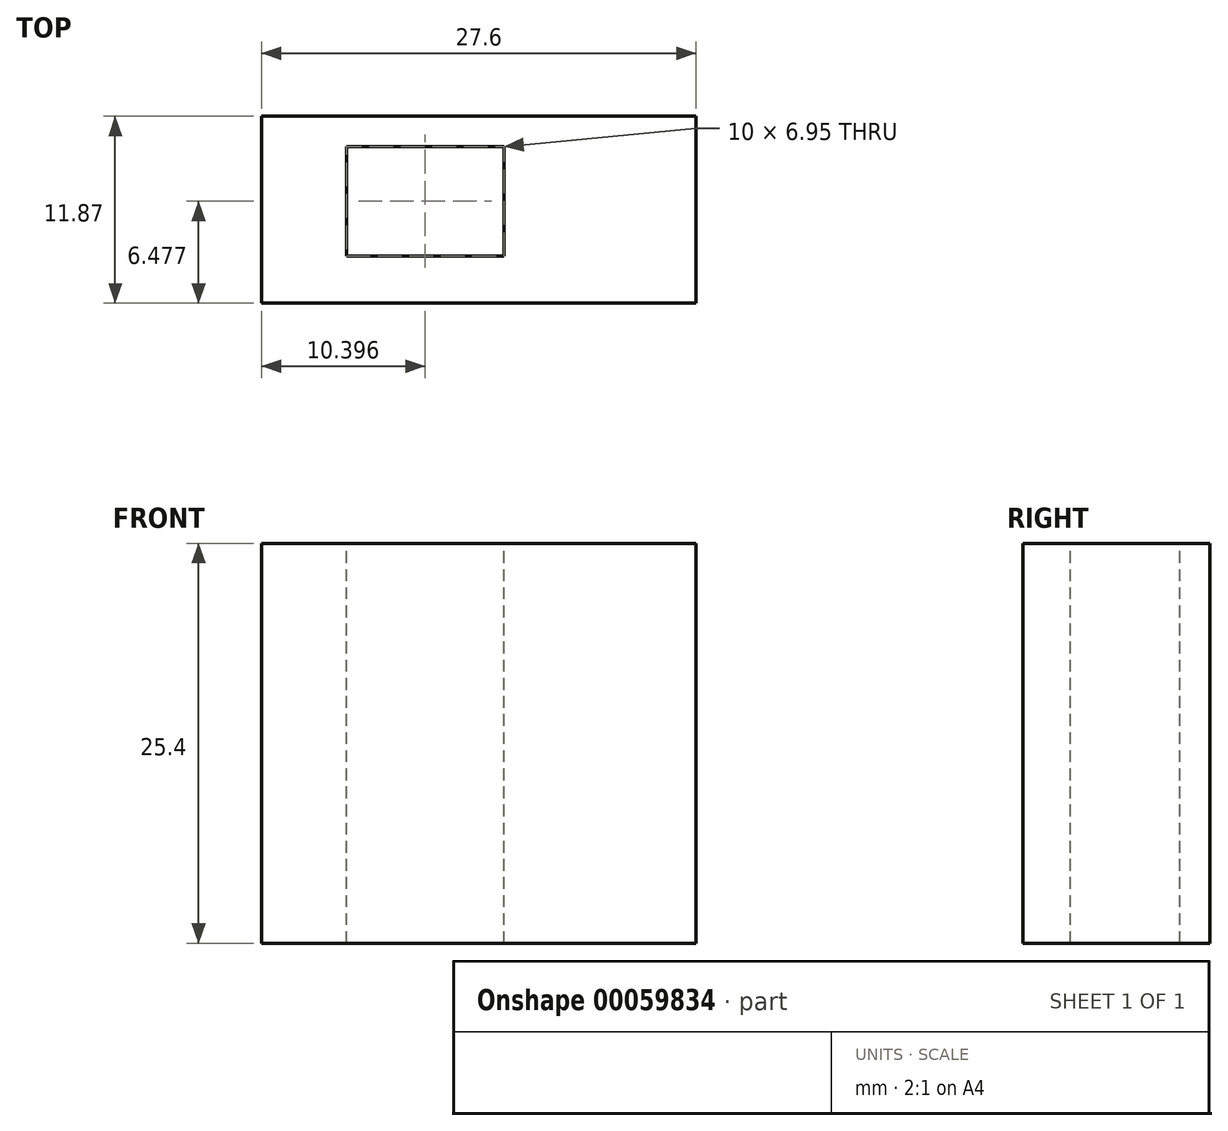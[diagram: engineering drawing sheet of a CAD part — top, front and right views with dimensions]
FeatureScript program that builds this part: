
annotation { "Feature Type Name" : "Feature", "Feature Type Description" : "" }
export const myFeature = defineFeature(function(context is Context, id is Id, definition is map)
    precondition{}
    {
        {
            var Q0;
            Q0=qCreatedBy(makeId("Top.planeOp"),FACE);
            var sketch = newSketch(context, id + "F0", { "sketchPlane" : qUnion([Q0])});
            skLineSegment(sketch, "E0.bottom", {"start": v(0, 0) * mm, "end": v(27.6, 0) * mm});
            skLineSegment(sketch, "E0.top", {"start": v(0, 11.87) * mm, "end": v(27.6, 11.87) * mm});
            skLineSegment(sketch, "E0.left", {"start": v(0, 0) * mm, "end": v(0, 11.87) * mm});
            skLineSegment(sketch, "E0.right", {"start": v(27.6, 0) * mm, "end": v(27.6, 11.87) * mm});
            skSolve(sketch);
        }
        {
            var Q0;
            Q0 = qSketchRegion(id + "F0", true);
            extrude(context, id + "F1", {"entities" : qUnion([Q0]), "depth" : 25.4 * mm});
        }
        {
            var Q0;
            Q0=makeQuery(id+"F1.opExtrude","CAP_FACE",FACE,{"disambiguationData":[OSD([sQuery(id+"F0.wireOp",EDGE,"E0.bottom"),sQuery(id+"F0.wireOp",EDGE,"E0.top"),sQuery(id+"F0.wireOp",EDGE,"E0.left"),sQuery(id+"F0.wireOp",EDGE,"E0.right")])],"isStart":false});
            var sketch = newSketch(context, id + "F3", { "sketchPlane" : qUnion([Q0])});
            skLineSegment(sketch, "E1.bottom", {"start": v(15.4, 3) * mm, "end": v(5.4, 3) * mm});
            skLineSegment(sketch, "E1.top", {"start": v(15.4, 9.95) * mm, "end": v(5.4, 9.95) * mm});
            skLineSegment(sketch, "E1.left", {"start": v(15.4, 3) * mm, "end": v(15.4, 9.95) * mm});
            skLineSegment(sketch, "E1.right", {"start": v(5.4, 3) * mm, "end": v(5.4, 9.95) * mm});
            skSolve(sketch);
        }
        {
            var Q0;
            Q0=makeQuery(id+"F3.imprint","IMPRINT",FACE,{"disambiguationData":[TD([[makeQuery(id+"F3.imprint","IMPRINT",EDGE,{"derivedFrom":sQuery(id+"F3.wireOp",EDGE,"E1.bottom")}),-1.0]])]});
            var sketch = newSketch(context, id + "F2", { "sketchPlane" : qUnion([Q0])});
            skSolve(sketch);
        }
        {
            var Q0;
            Q0=makeQuery(id+"F2.imprint","IMPRINT",FACE,{"disambiguationData":[TD([[makeQuery(id+"F2.imprint","IMPRINT",EDGE,{"derivedFrom":makeQuery(id+"F3.imprint","IMPRINT",EDGE,{"derivedFrom":sQuery(id+"F3.wireOp",EDGE,"E1.bottom")})}),-1.0]])]});
            extrude(context, id + "F4", {"entities" : qUnion([Q0]), "operationType" : NewBodyOperationType.REMOVE, "endBound" : BoundingType.THROUGH_ALL, "oppositeDirection" : true, "depth" : 25 * mm});
        }
    });
